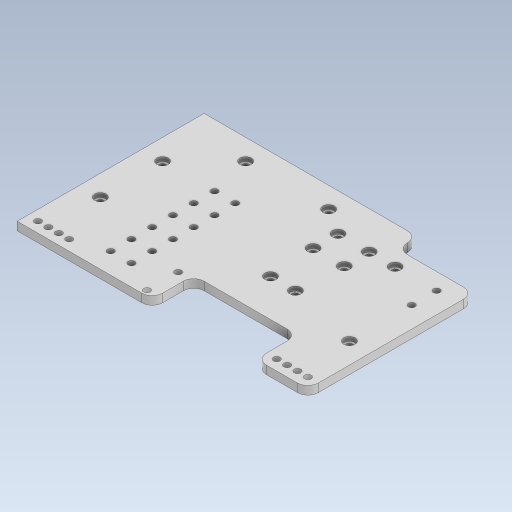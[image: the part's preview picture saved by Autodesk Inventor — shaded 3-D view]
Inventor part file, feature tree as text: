
AUTODESK INVENTOR PART (.ipt)
format: ipt  version: 2023.5 (Build 275446000, 446)  size: 501,248 bytes
history: native  units: mm
features: extrude x2, sketch x1, fillet x1
ambient origin geometry x8: Origin, YZ Plane, XZ Plane, XY Plane, X Axis, Y Axis, Z Axis, Center Point
bodies: Solid1 (feature_tree)
feature tree (4):
  sketch  "Sketch1"  dims[d29=90.0mm d30=140.0mm d31=3.2mm d32=30.0mm d33=10.0mm d34=5.5mm d35=3.2mm d36=5.5mm d37=4.0mm d38=0.0mm d39=2.0mm d40=0.0mm d41=10.0mm d42=10.0mm d43=10.0mm d44=10.0mm d45=10.0mm d46=3.2mm d47=5.0mm d48=2.5mm d49=3.2mm d50=15.0mm d51=3.2mm d53=20.0mm d61=3.2mm d62=10.0mm d63=3.2mm d64=10.0mm d65=3.2mm d66=10.0mm d67=10.0mm d68=3.2mm d69=10.0mm d70=3.2mm d71=10.0mm d72=3.2mm d73=3.2mm d74=3.2mm d75=10.0mm d76=3.2mm d77=10.0mm d78=3.2mm d79=3.2mm d80=3.3mm d81=5.0mm d82=5.0mm d83=3.2mm d84=5.5mm d85=3.2mm d86=3.2mm d87=10.0mm]
  extrude  "Extrusion1"  Depth=140.0mm
  extrude  "Extrusion2"  Depth=10.0mm
  fillet  "Fillet1"  Radius=30.0mm
